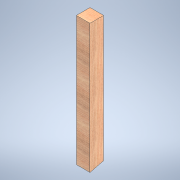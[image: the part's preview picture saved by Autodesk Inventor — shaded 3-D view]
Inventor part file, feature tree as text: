
AUTODESK INVENTOR PART (.ipt)
format: ipt  version: 2020.2 (Build 242310000, 310)  size: 105,984 bytes
history: native  units: in
note: dims shown in document units (in); Inventor stores cm internally (conversion verified against a paired STEP export)
features: extrude x1, sketch x1
ambient origin geometry x8: Origin, YZ Plane, XZ Plane, XY Plane, X Axis, Y Axis, Z Axis, Center Point
bodies: Solid1 (feature_tree)
feature tree (2):
  extrude  "Extrusion1"  TaperAngle=0.0deg  [1 undecoded]
  sketch  "Sketch1"  dims[d3=3.5in d4=0.0in]
note: 1 required parameter value undecoded (feature->parameter linkage not recoverable at this tier; creation-order binding heuristic only, values carry confidence <= 0.55)
